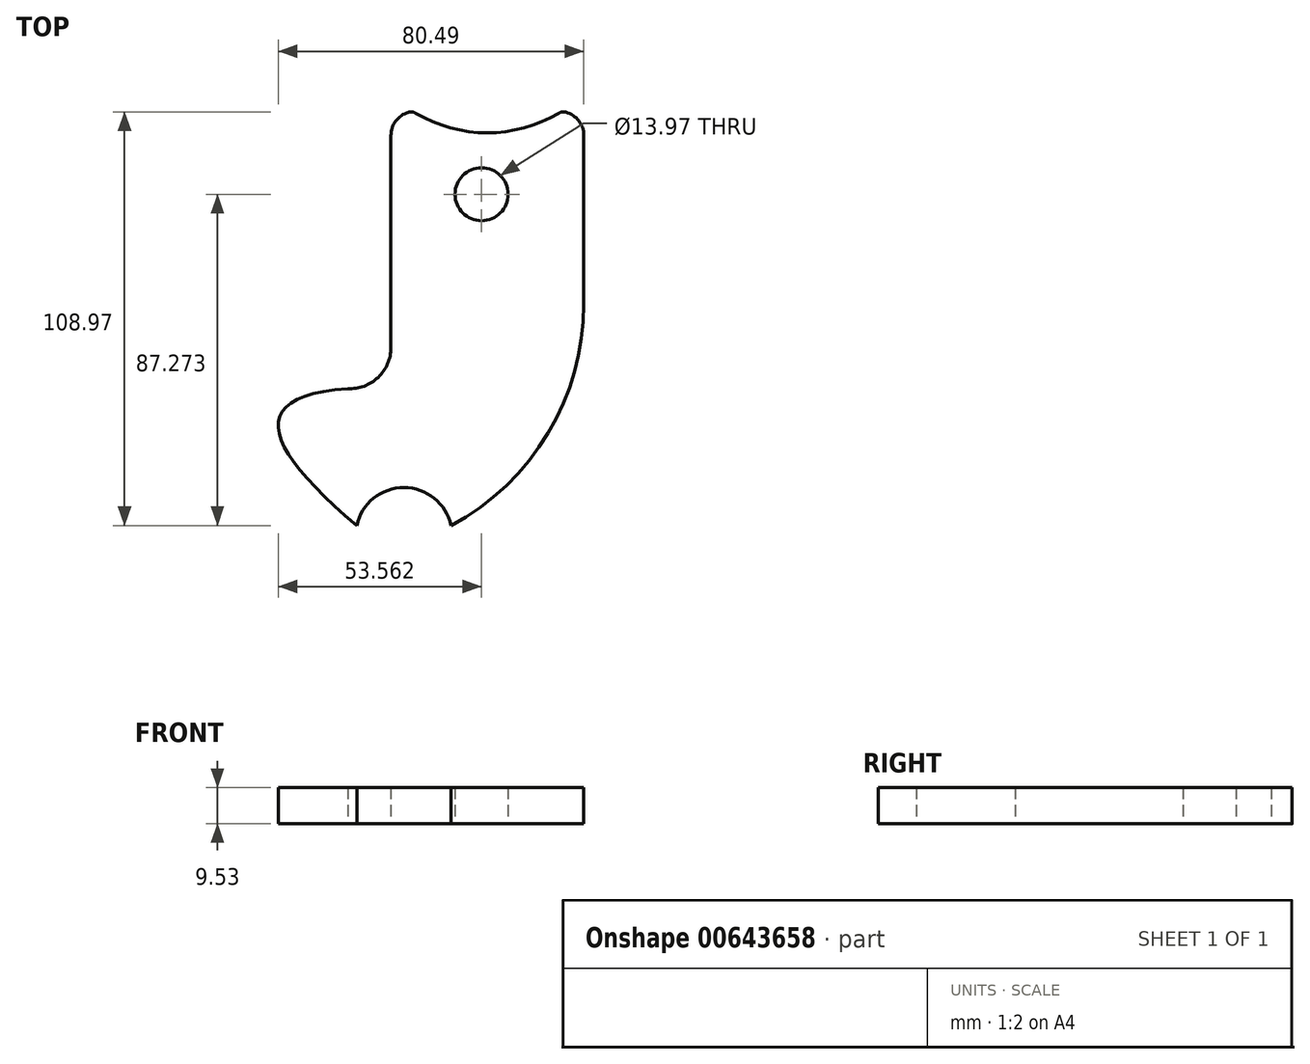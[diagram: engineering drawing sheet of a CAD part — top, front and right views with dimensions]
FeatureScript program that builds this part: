
annotation { "Feature Type Name" : "Feature", "Feature Type Description" : "" }
export const myFeature = defineFeature(function(context is Context, id is Id, definition is map)
    precondition{}
    {
        {
            var Q0;
            Q0=qCreatedBy(makeId("Top.planeOp"),FACE);
            var sketch = newSketch(context, id + "F0", { "sketchPlane" : qUnion([Q0])});
            skLineSegment(sketch, "E0", {"start": v(-4.5, 26.29) * mm, "end": v(-4.5, 82.17) * mm});
            skLineSegment(sketch, "E1", {"start": v(46.3, 82.17) * mm, "end": v(46.3, 54.61) * mm});
            skArc(sketch, "E2", {"start": v(11.34, -20.58) * mm, "mid": v(-1.08, -10.54) * mm, "end": v(-13.5, -20.58) * mm});
            skArc(sketch, "E3", {"start": v(-15.9, 15.5) * mm, "mid": v(-7.88, 18.44) * mm, "end": v(-4.5, 26.29) * mm});
            skFitSpline(sketch, "E4", {"points": [v(-15.9, 15.5) * mm, v(-13.5, -20.58) * mm], "startDerivative": vector(-81.98, -5.77) * mm, "endDerivative": vector(73.14, -61.75) * mm});
            skPoint(sketch, "E5.visualSharp", {"position": v(-4.5, 88.52) * mm});
            skArc(sketch, "E5.filletArc", {"start": v(0.1, 88.27) * mm, "mid": v(-3.23, 85.99) * mm, "end": v(-4.5, 82.17) * mm});
            skPoint(sketch, "E6.visualSharp", {"position": v(46.3, 88.52) * mm});
            skArc(sketch, "E6.filletArc", {"start": v(46.3, 82.17) * mm, "mid": v(44.98, 86.04) * mm, "end": v(41.58, 88.3) * mm});
            skLineSegment(sketch, "E7", {"start": v(46.3, 82.17) * mm, "end": v(46.3, 37.72) * mm});
            skArc(sketch, "E8", {"start": v(11.34, -20.58) * mm, "mid": v(36.89, 3.73) * mm, "end": v(46.3, 37.72) * mm});
            skPoint(sketch, "E9.visualSharp", {"position": v(11.34, -20.58) * mm});
            skArc(sketch, "E10", {"start": v(2.1, 88.01) * mm, "mid": v(20.86, 82.87) * mm, "end": v(39.63, 88.03) * mm});
            skPoint(sketch, "E11.visualSharp", {"position": v(1.3, 88.5) * mm});
            skArc(sketch, "E11.filletArc", {"start": v(2.1, 88.01) * mm, "mid": v(1.12, 88.35) * mm, "end": v(0.1, 88.27) * mm});
            skPoint(sketch, "E12.visualSharp", {"position": v(40.4, 88.5) * mm});
            skArc(sketch, "E12.filletArc", {"start": v(41.58, 88.3) * mm, "mid": v(40.58, 88.36) * mm, "end": v(39.63, 88.03) * mm});
            skLineSegment(sketch, "E13", {"start": v(-4.5, 88.52) * mm, "end": v(72.42, 88.27) * mm, "construction": true});
            skCircle(sketch, "E14", {"center": v(19.37, 66.7) * mm, "radius": 6.99 * mm});
            skSolve(sketch);
        }
        {
            var Q0;
            Q0=makeQuery(id+"F0.imprint","IMPRINT",FACE,{"disambiguationData":[TD([[makeQuery(id+"F0.imprint","IMPRINT",EDGE,{"derivedFrom":sQuery(id+"F0.wireOp",EDGE,"E0")}),-1.0]])]});
            extrude(context, id + "F1", {"entities" : qUnion([Q0]), "depth" : 9.52 * mm, "offsetDistance" : 25.4 * mm});
        }
    });
